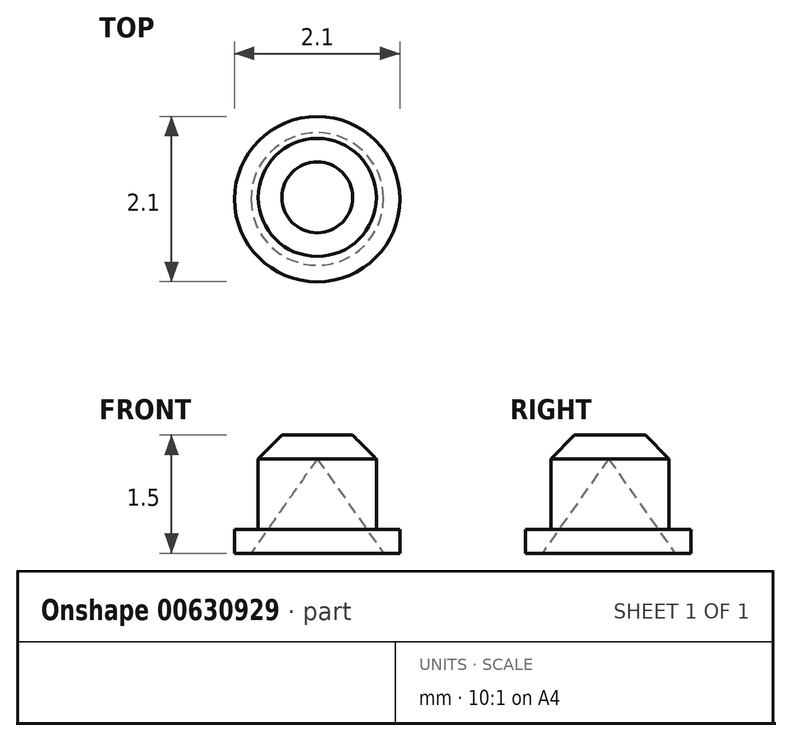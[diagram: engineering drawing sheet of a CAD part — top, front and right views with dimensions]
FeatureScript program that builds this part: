
annotation { "Feature Type Name" : "Feature", "Feature Type Description" : "" }
export const myFeature = defineFeature(function(context is Context, id is Id, definition is map)
    precondition{}
    {
        {
            var Q0;
            Q0=qCreatedBy(makeId("Top.planeOp"),FACE);
            var sketch = newSketch(context, id + "F0", { "sketchPlane" : qUnion([Q0])});
            skCircle(sketch, "E0", {"center": v(0, 0) * mm, "radius": 0.75 * mm});
            skSolve(sketch);
        }
        {
            var Q0;
            Q0=makeQuery(id+"F0.imprint","IMPRINT",FACE,{"disambiguationData":[TD([[makeQuery(id+"F0.imprint","IMPRINT",EDGE,{"derivedFrom":sQuery(id+"F0.wireOp",EDGE,"E0")}),1.0]])]});
            extrude(context, id + "F1", {"entities" : qUnion([Q0]), "depth" : 1.2 * mm, "offsetDistance" : 25 * mm});
        }
        {
            var Q0;
            Q0=makeQuery(id+"F1.opExtrude","CAP_FACE",FACE,{"disambiguationData":[OSD([sQuery(id+"F0.wireOp",EDGE,"E0")])],"isStart":true});
            var sketch = newSketch(context, id + "F2", { "sketchPlane" : qUnion([Q0])});
            skCircle(sketch, "E1", {"center": v(0, 0.02) * mm, "radius": 1.05 * mm});
            skSolve(sketch);
        }
        {
            var Q0;
            Q0=makeQuery(id+"F2.imprint","IMPRINT",FACE,{"disambiguationData":[TD([[makeQuery(id+"F2.imprint","IMPRINT",EDGE,{"derivedFrom":sQuery(id+"F2.wireOp",EDGE,"E1")}),1.0]])]});
            extrude(context, id + "F3", {"entities" : qUnion([Q0]), "operationType" : NewBodyOperationType.ADD, "depth" : -0.3 * mm, "offsetDistance" : 25 * mm});
        }
        {
            var Q0;
            Q0=makeQuery(id+"F1.opExtrude","CAP_FACE",FACE,{"disambiguationData":[OSD([sQuery(id+"F0.wireOp",EDGE,"E0")])],"isStart":false});
            extrude(context, id + "F4", {"entities" : qUnion([Q0]), "operationType" : NewBodyOperationType.ADD, "depth" : 0.3 * mm, "offsetDistance" : 25 * mm});
        }
        {
            var Q0;
            Q0=makeQuery(id+"F4.opExtrude","CAP_EDGE",EDGE,{"disambiguationData":[OSD([sQuery(id+"F0.wireOp",EDGE,"E0")])],"isStart":false});
            chamfer(context, id + "F5", {"entities" : qUnion([Q0]), "width" : 0.3 * mm, "tangentPropagation" : true});
        }
        {
            var Q0;
            Q0=qCreatedBy(makeId("Front.planeOp"),FACE);
            var sketch = newSketch(context, id + "F6", { "sketchPlane" : qUnion([Q0])});
            skLineSegment(sketch, "E2", {"start": v(0, 0) * mm, "end": v(0, -1.21) * mm});
            skLineSegment(sketch, "E3", {"start": v(0, -1.21) * mm, "end": v(-0.85, -1.21) * mm});
            skLineSegment(sketch, "E4", {"start": v(-0.85, -1.21) * mm, "end": v(0, 0) * mm});
            skSolve(sketch);
        }
        {
            var Q0;
            Q0=makeQuery(id+"F6.imprint","IMPRINT",FACE,{"disambiguationData":[TD([[makeQuery(id+"F6.imprint","IMPRINT",EDGE,{"derivedFrom":sQuery(id+"F6.wireOp",EDGE,"E2")}),-1.0]])]});
            var Q1;
            Q1=sQuery(id+"F6.wireOp",EDGE,"E2");
            revolve(context, id + "F7", {"entities" : qUnion([Q0]), "axis" : qUnion([Q1]), "revolveType" : RevolveType.FULL});
        }
        {
            var Q0;
            Q0=makeQuery(id+"F7.opRevolve","SWEPT_BODY",BODY,{"disambiguationData":[OSD([sQuery(id+"F6.wireOp",EDGE,"E2"),sQuery(id+"F6.wireOp",EDGE,"E3"),sQuery(id+"F6.wireOp",EDGE,"E4")])]});
            var Q1;
            Q1=qCreatedBy(makeId("Origin.pointOp"),VERTEX);
            transform(context, id + "F8", {"entities" : qUnion([Q0]), "transformType" : TransformType.TRANSLATION_3D, "dx" : 0 * mm, "dy" : 0 * mm, "dz" : 1 * mm, "makeCopy" : false});
        }
        {
            var Q0;
            Q0=makeQuery(id+"F7.opRevolve","SWEPT_BODY",BODY,{"disambiguationData":[OSD([sQuery(id+"F6.wireOp",EDGE,"E2"),sQuery(id+"F6.wireOp",EDGE,"E3"),sQuery(id+"F6.wireOp",EDGE,"E4")])]});
            transform(context, id + "F9", {"entities" : qUnion([Q0]), "transformType" : TransformType.TRANSLATION_3D, "dx" : 0 * mm, "dy" : 0 * mm, "dz" : 0.2 * mm, "makeCopy" : false});
        }
        {
            var Q0;
            Q0=makeQuery(id+"F7.opRevolve","SWEPT_BODY",BODY,{"disambiguationData":[OSD([sQuery(id+"F6.wireOp",EDGE,"E2"),sQuery(id+"F6.wireOp",EDGE,"E3"),sQuery(id+"F6.wireOp",EDGE,"E4")])]});
            transform(context, id + "F10", {"entities" : qUnion([Q0]), "transformType" : TransformType.TRANSLATION_3D, "dx" : 0 * mm, "dy" : -0.02 * mm, "dz" : 0 * mm, "makeCopy" : false});
        }
        {
            var Q0;
            Q0=makeQuery(id+"F7.opRevolve","SWEPT_BODY",BODY,{"disambiguationData":[OSD([sQuery(id+"F6.wireOp",EDGE,"E2"),sQuery(id+"F6.wireOp",EDGE,"E3"),sQuery(id+"F6.wireOp",EDGE,"E4")])]});
            var Q1;
            Q1=makeQuery(id+"F1.opExtrude","SWEPT_BODY",BODY,{"disambiguationData":[OSD([sQuery(id+"F0.wireOp",EDGE,"E0")])]});
            booleanBodies(context, id + "F11", {"operationType" : BooleanOperationType.SUBTRACTION, "tools" : qUnion([Q0]), "targets" : qUnion([Q1])});
        }
    });
